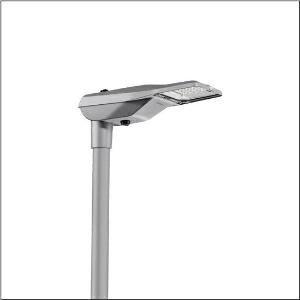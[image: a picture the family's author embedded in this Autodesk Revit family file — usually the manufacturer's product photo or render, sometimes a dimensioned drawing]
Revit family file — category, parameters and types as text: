
# Revit family: streetlight_sl_21_micro___stw1_0a_5xe1e33t08db_9129
name_source: partatom
category: Lighting Fixtures
units: mm (PartAtom-declared; Revit-internal decimal feet)

## family parameters
Cut with Voids When Loaded = No
Host = Face
Light Source = No
Part Type = Normal
Room Calculation Point = No
Round Connector Dimension = Use Diameter
Shared = No

## types (1)
- --- (1 x LED, 5110 lm, 39.1 W, 3000K)
    Apparent Load = 39 VA
    CIE Flux Codes = 38 75 98 100 100
    Color Rendering = 70
    Color Temperature = 3000K
    Default Elevation = 1800 mm
    Description = Streetlight SL 21 micro, mast luminaire, primary light control with lens, of PMMA, primary optical cover: cover, of toughened safety glass, transparent, light distribution: STW1.0a, light emission: direct distribution, primary light characteristic: asymmetric, installation type: side-entry, post-top, LED, High Power LED, rated luminous flux: 5.110lm, luminous efficacy: 131lm/W, light colour: 730, colour temperature: 3000K, control: flexible luminous flux parameterisation, time-dependent luminous flux control, constant luminous flux control, overheat protection, pre-setting: logarithmic dimming characteristic, mains connection: 220..240V, AC, 50/60Hz, start of lifetime: 39W, end of service life: 41W, reduction: 18W, luminaire housing, of diecast aluminium, powder-coated, Siteco® metallic grey (DB 702S), corrosivity category C5 mid according to DIN EN ISO 12944, please order mast flange separately, inclination adjustable: 0°, 5°, 10°, 15°, sealing non-destructively replaceable, multi-level sealing system, length: 528mm, width: 235mm, height: 110mm, mast flange for spigot size: 42mm (side-entry): 5XC10008XM4, 60/48mm (side-entry/post-top): 5XC10108XM2, 76/60mm (side-entry/post-top): 5XC10108XM1, Smart Interface below and above, protection rating (complete): IP66, insulation class (complete): insulation class II (safety insulation), certification: CE, ENEC, ENEC+, VDE, impact resistance: IK09, permissible operating ambient temperature for outdoor applications: -40..+50°C, standard-compliant lighting for roads and squares, packaging unit: 1 piece

Light Distribution: STW1.0a
    Height = 110 mm
    Lamp = 1 x LED
    Lamp Light Flux = 5110 lm
    Lamp Power = 39.1 W
    Lamp count = 1
    Length = 528 mm
    Luminous efficacy = 131 lm/W
    Manufacturer = Siteco
    ModVariant = No
    Model = 5XE1E33T08DB
    Number of Poles = 1
    OnlyDefault = Yes
    Power Factor = 1
    Product Name = Streetlight SL 21 micro | STW1.0a
    Product group = mast luminaire | pylon top
    ProductGroupID = 6100
    Protection Class = Protection class II
    Protection Degree = IP 66
    RLX_Detail_Level = 1
    RLX_Emergency_Light_Flux = 0 lm
    RLX_Emergency_Type = 0
    RLX_Emergency_Type_DB = No
    RlxData = <blob elided: 98513 chars, md5=b3e494ed>
    Socket = socket
    Standby Power = 0 W
    System Light Flux = 5110 lm
    System Power = 39 W
    Type Comments = factory setting: luminous flux: 100 % | dim-lin: 254 | 765 mA
    Type Image = l_1007239.jpg
    URL = http://relux.com
    VarID = @adj_125643
    Voltage = 0 V
    Weight = 0.00 kg
    Width = 235 mm

## geometry (parser evidence)
native form markers: Blend x4, Sweep x11
no freeform markers — native parametric forms only
